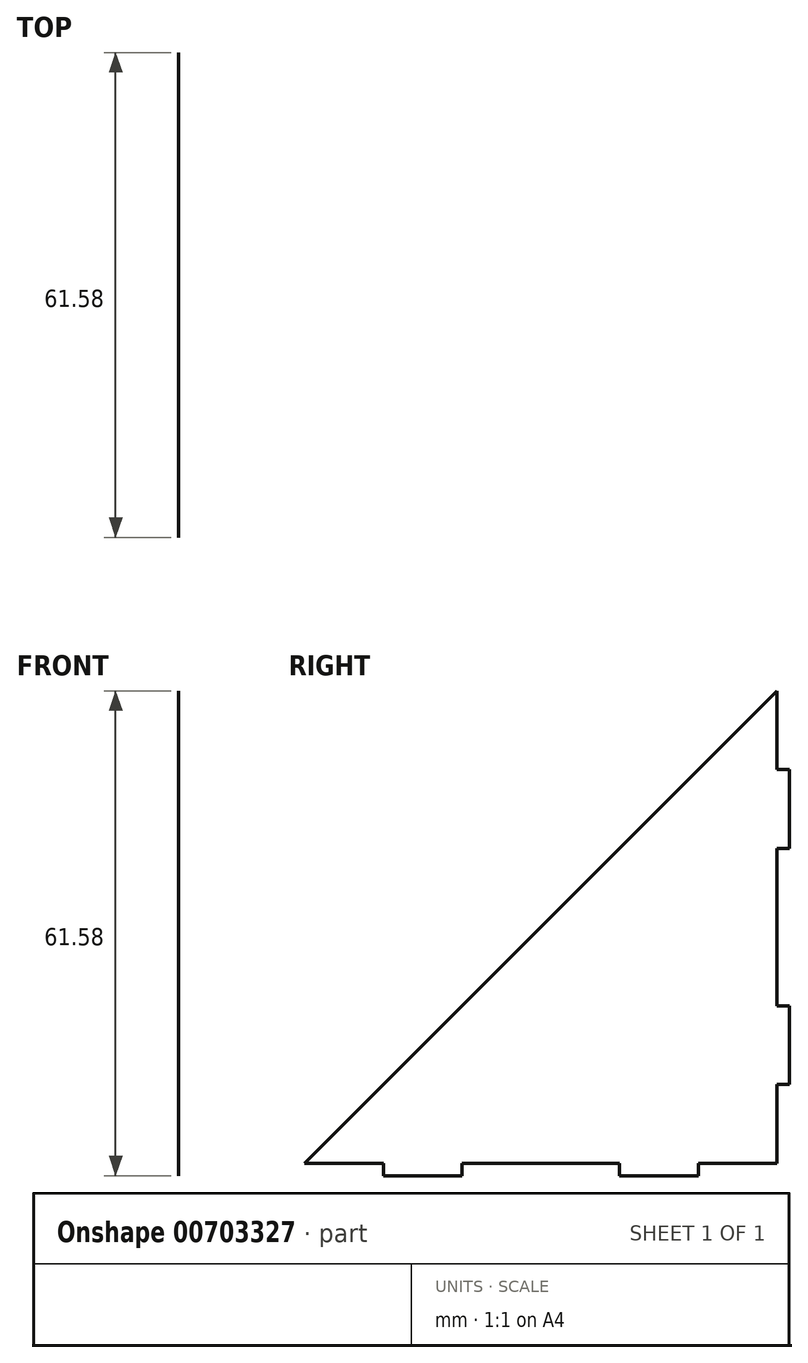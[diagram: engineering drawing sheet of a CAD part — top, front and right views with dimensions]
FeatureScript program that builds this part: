
annotation { "Feature Type Name" : "Feature", "Feature Type Description" : "" }
export const myFeature = defineFeature(function(context is Context, id is Id, definition is map)
    precondition{}
    {
        {
            var Q0;
            Q0=qCreatedBy(makeId("Right.planeOp"),FACE);
            var sketch = newSketch(context, id + "F0", { "sketchPlane" : qUnion([Q0])});
            skLineSegment(sketch, "E0", {"start": v(-44.42, -15.58) * mm, "end": v(15.58, -15.58) * mm});
            skLineSegment(sketch, "E1", {"start": v(15.58, -15.58) * mm, "end": v(15.58, 44.42) * mm});
            skLineSegment(sketch, "E2", {"start": v(15.58, 44.42) * mm, "end": v(-44.42, -15.58) * mm});
            skLineSegment(sketch, "E3", {"start": v(-24.42, -17.16) * mm, "end": v(-24.42, -15.58) * mm});
            skLineSegment(sketch, "E4", {"start": v(-4.42, -17.16) * mm, "end": v(-4.42, -15.58) * mm});
            skLineSegment(sketch, "E5", {"start": v(17.16, 4.42) * mm, "end": v(15.58, 4.42) * mm});
            skLineSegment(sketch, "E6", {"start": v(17.16, 24.42) * mm, "end": v(15.58, 24.42) * mm});
            skLineSegment(sketch, "E7", {"start": v(-24.42, -17.16) * mm, "end": v(-34.42, -17.16) * mm});
            skLineSegment(sketch, "E8", {"start": v(-34.42, -17.16) * mm, "end": v(-34.42, -15.58) * mm});
            skLineSegment(sketch, "E9", {"start": v(-4.42, -17.16) * mm, "end": v(5.58, -17.16) * mm});
            skLineSegment(sketch, "E10", {"start": v(5.58, -17.16) * mm, "end": v(5.58, -15.58) * mm});
            skLineSegment(sketch, "E11", {"start": v(17.16, 4.42) * mm, "end": v(17.16, -5.58) * mm});
            skLineSegment(sketch, "E12", {"start": v(17.16, -5.58) * mm, "end": v(15.58, -5.58) * mm});
            skLineSegment(sketch, "E13", {"start": v(17.16, 24.42) * mm, "end": v(17.16, 34.42) * mm});
            skLineSegment(sketch, "E14", {"start": v(17.16, 34.42) * mm, "end": v(15.58, 34.42) * mm});
            skSolve(sketch);
        }
        {
            var Q0;
            Q0 = qSketchRegion(id + "F0", true);
            extrude(context, id + "F1", {"entities" : qUnion([Q0]), "depth" : 1 / 406.4 * mm, "offsetDistance" : 25 * mm});
        }
    });
